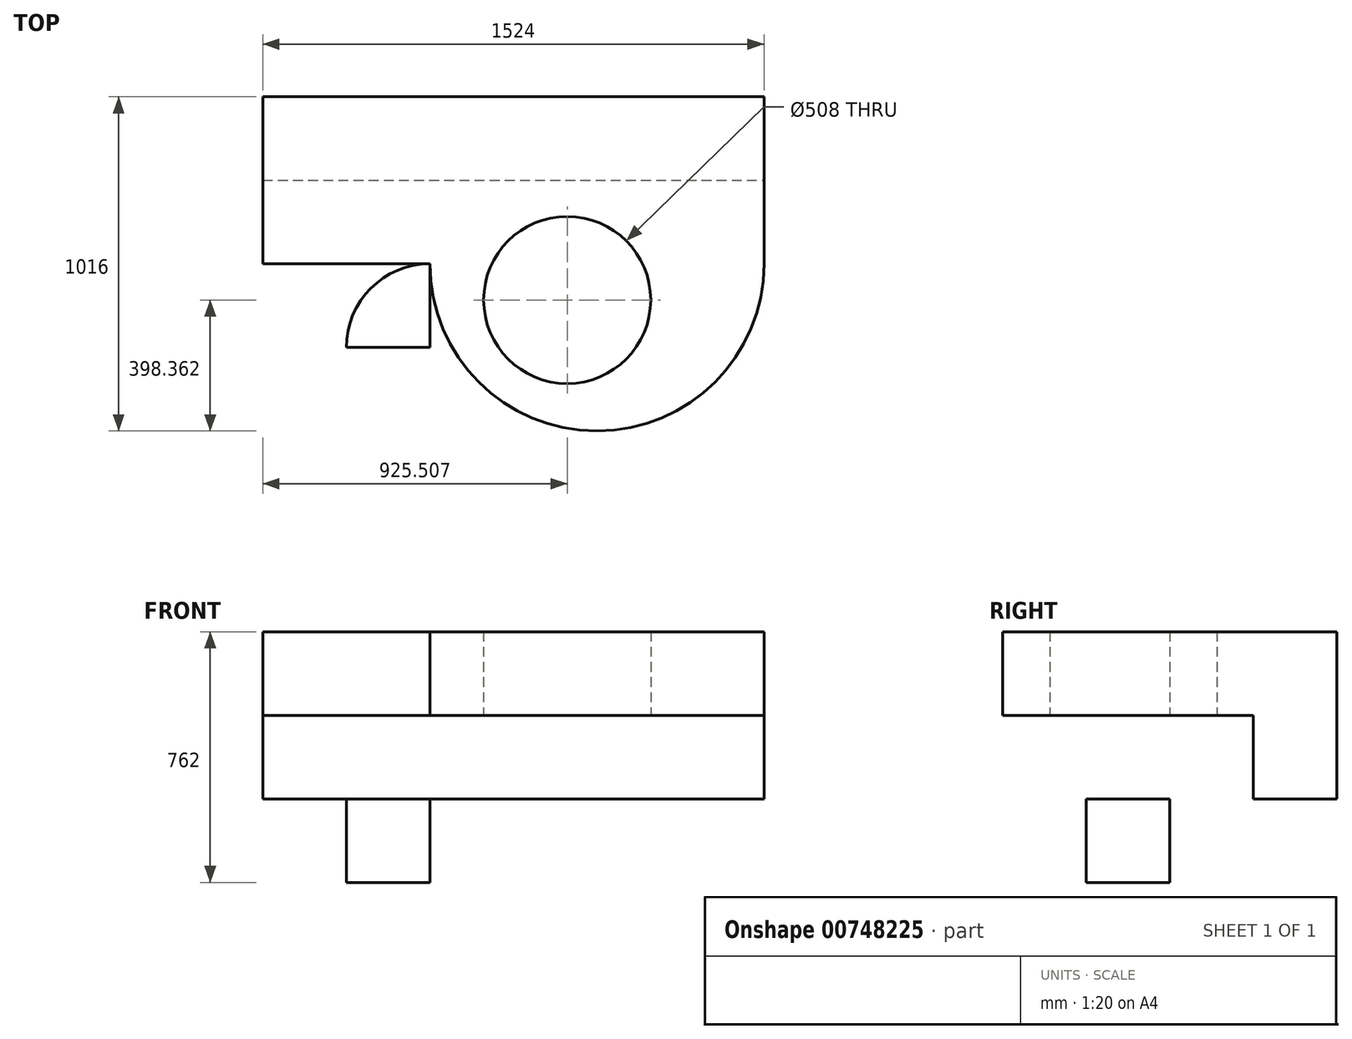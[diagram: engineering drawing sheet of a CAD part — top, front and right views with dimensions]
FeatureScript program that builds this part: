
annotation { "Feature Type Name" : "Feature", "Feature Type Description" : "" }
export const myFeature = defineFeature(function(context is Context, id is Id, definition is map)
    precondition{}
    {
        {
            var Q0;
            Q0=qCreatedBy(makeId("Front.planeOp"),FACE);
            var sketch = newSketch(context, id + "F0", { "sketchPlane" : qUnion([Q0])});
            skLineSegment(sketch, "E0", {"start": v(0, -508) * mm, "end": v(508, -508) * mm});
            skLineSegment(sketch, "E1", {"start": v(508, -508) * mm, "end": v(508, -762) * mm});
            skLineSegment(sketch, "E2", {"start": v(508, -762) * mm, "end": v(1524, -762) * mm});
            skLineSegment(sketch, "E3", {"start": v(1524, -762) * mm, "end": v(1524, 0) * mm});
            skLineSegment(sketch, "E4", {"start": v(1524, 0) * mm, "end": v(0, 0) * mm});
            skLineSegment(sketch, "E5", {"start": v(0, 0) * mm, "end": v(0, -508) * mm});
            skLineSegment(sketch, "E6", {"start": v(508, -762) * mm, "end": v(0, -762) * mm});
            skLineSegment(sketch, "E7", {"start": v(0, -762) * mm, "end": v(0, -508) * mm});
            skSolve(sketch);
        }
        {
            var Q0;
            Q0=makeQuery(id+"F0.imprint","IMPRINT",FACE,{"disambiguationData":[TD([[makeQuery(id+"F0.imprint","IMPRINT",EDGE,{"derivedFrom":sQuery(id+"F0.wireOp",EDGE,"E0")}),1.0]])]});
            extrude(context, id + "F1", {"entities" : qUnion([Q0]), "depth" : 254 * mm, "offsetDistance" : 25.4 * mm});
        }
        {
            var Q0;
            Q0=makeQuery(id+"F0.imprint","IMPRINT",FACE,{"disambiguationData":[TD([[makeQuery(id+"F0.imprint","IMPRINT",EDGE,{"derivedFrom":sQuery(id+"F0.wireOp",EDGE,"E0")}),-1.0]])]});
            extrude(context, id + "F2", {"entities" : qUnion([Q0]), "operationType" : NewBodyOperationType.ADD, "depth" : 762 * mm, "offsetDistance" : 25.4 * mm});
        }
        {
            var Q0;
            Q0=makeQuery(id+"F2.boolean.opBoolean","MERGE",FACE,{"derivedFrom":[makeQuery(id+"F1.opExtrude","SWEPT_FACE",FACE,{"disambiguationData":[OSD([sQuery(id+"F0.wireOp",EDGE,"E2")])]}),makeQuery(id+"F2.opExtrude","SWEPT_FACE",FACE,{"disambiguationData":[OSD([sQuery(id+"F0.wireOp",EDGE,"E6")])]})]});
            var sketch = newSketch(context, id + "F3", { "sketchPlane" : qUnion([Q0])});
            skArc(sketch, "E8", {"start": v(508, 508) * mm, "mid": v(328.4, 582.4) * mm, "end": v(254, 762) * mm});
            skSolve(sketch);
        }
        {
            var Q0;
            {var subQ0=sQuery(id+"F3.wireOp",EDGE,"E8");Q0=makeQuery(id+"F3.imprint","IMPRINT",FACE,{"disambiguationData":[TD([[makeQuery(id+"F3.imprint","IMPRINT",EDGE,{"derivedFrom":subQ0}),-1.0]])]});}
            extrude(context, id + "F4", {"entities" : qUnion([Q0]), "operationType" : NewBodyOperationType.REMOVE, "oppositeDirection" : true, "depth" : 254 * mm, "offsetDistance" : 25.4 * mm});
        }
        {
            var Q0;
            Q0=makeQuery(id+"F1.opExtrude","CAP_FACE",FACE,{"disambiguationData":[OSD([sQuery(id+"F0.wireOp",EDGE,"E0"),sQuery(id+"F0.wireOp",EDGE,"E1"),sQuery(id+"F0.wireOp",EDGE,"E2"),sQuery(id+"F0.wireOp",EDGE,"E3"),sQuery(id+"F0.wireOp",EDGE,"E4"),sQuery(id+"F0.wireOp",EDGE,"E5")])],"isStart":false});
            var sketch = newSketch(context, id + "F5", { "sketchPlane" : qUnion([Q0])});
            skLineSegment(sketch, "E9", {"start": v(0, 0) * mm, "end": v(0, -254) * mm});
            skLineSegment(sketch, "E10", {"start": v(0, -254) * mm, "end": v(1524, -254) * mm});
            skLineSegment(sketch, "E11", {"start": v(1524, -254) * mm, "end": v(1524, 0) * mm});
            skLineSegment(sketch, "E12", {"start": v(1524, 0) * mm, "end": v(0, 0) * mm});
            skSolve(sketch);
        }
        {
            var Q0;
            Q0 = qSketchRegion(id + "F5", true);
            extrude(context, id + "F6", {"entities" : qUnion([Q0]), "operationType" : NewBodyOperationType.ADD, "depth" : 254 * mm, "offsetDistance" : 25.4 * mm});
        }
        {
            var Q0;
            Q0=makeQuery(id+"F6.opExtrude","SWEPT_FACE",FACE,{"disambiguationData":[OSD([sQuery(id+"F5.wireOp",EDGE,"E10")])]});
            var sketch = newSketch(context, id + "F7", { "sketchPlane" : qUnion([Q0])});
            skArc(sketch, "E13", {"start": v(1524, 508) * mm, "mid": v(1016, 1016) * mm, "end": v(508, 508) * mm});
            skSolve(sketch);
        }
        {
            var Q0;
            {var subQ0=sQuery(id+"F7.wireOp",EDGE,"E13");Q0=makeQuery(id+"F7.imprint","IMPRINT",FACE,{"disambiguationData":[TD([[makeQuery(id+"F7.imprint","IMPRINT",EDGE,{"derivedFrom":subQ0}),1.0]])]});}
            extrude(context, id + "F8", {"entities" : qUnion([Q0]), "operationType" : NewBodyOperationType.ADD, "oppositeDirection" : true, "depth" : 254 * mm, "offsetDistance" : 25.4 * mm});
        }
        {
            var Q0;
            {var subQ0=sQuery(id+"F5.wireOp",EDGE,"E10");Q0=makeQuery(id+"F8.boolean.opBoolean","MERGE",FACE,{"derivedFrom":[makeQuery(id+"F6.opExtrude","SWEPT_FACE",FACE,{"disambiguationData":[OSD([subQ0])]}),makeQuery(id+"F8.opExtrude","CAP_FACE",FACE,{"disambiguationData":[OSD([subQ0,sQuery(id+"F7.wireOp",EDGE,"E13")])],"isStart":true})]});}
            var sketch = newSketch(context, id + "F9", { "sketchPlane" : qUnion([Q0])});
            skCircle(sketch, "E14", {"center": v(925.5, 617.64) * mm, "radius": 254 * mm});
            skSolve(sketch);
        }
        {
            var Q0;
            Q0=makeQuery(id+"F9.imprint","IMPRINT",FACE,{"disambiguationData":[TD([[makeQuery(id+"F9.imprint","IMPRINT",EDGE,{"derivedFrom":sQuery(id+"F9.wireOp",EDGE,"E14")}),1.0]])]});
            extrude(context, id + "F10", {"entities" : qUnion([Q0]), "operationType" : NewBodyOperationType.REMOVE, "oppositeDirection" : true, "depth" : 254 * mm, "offsetDistance" : 25.4 * mm});
        }
    });
